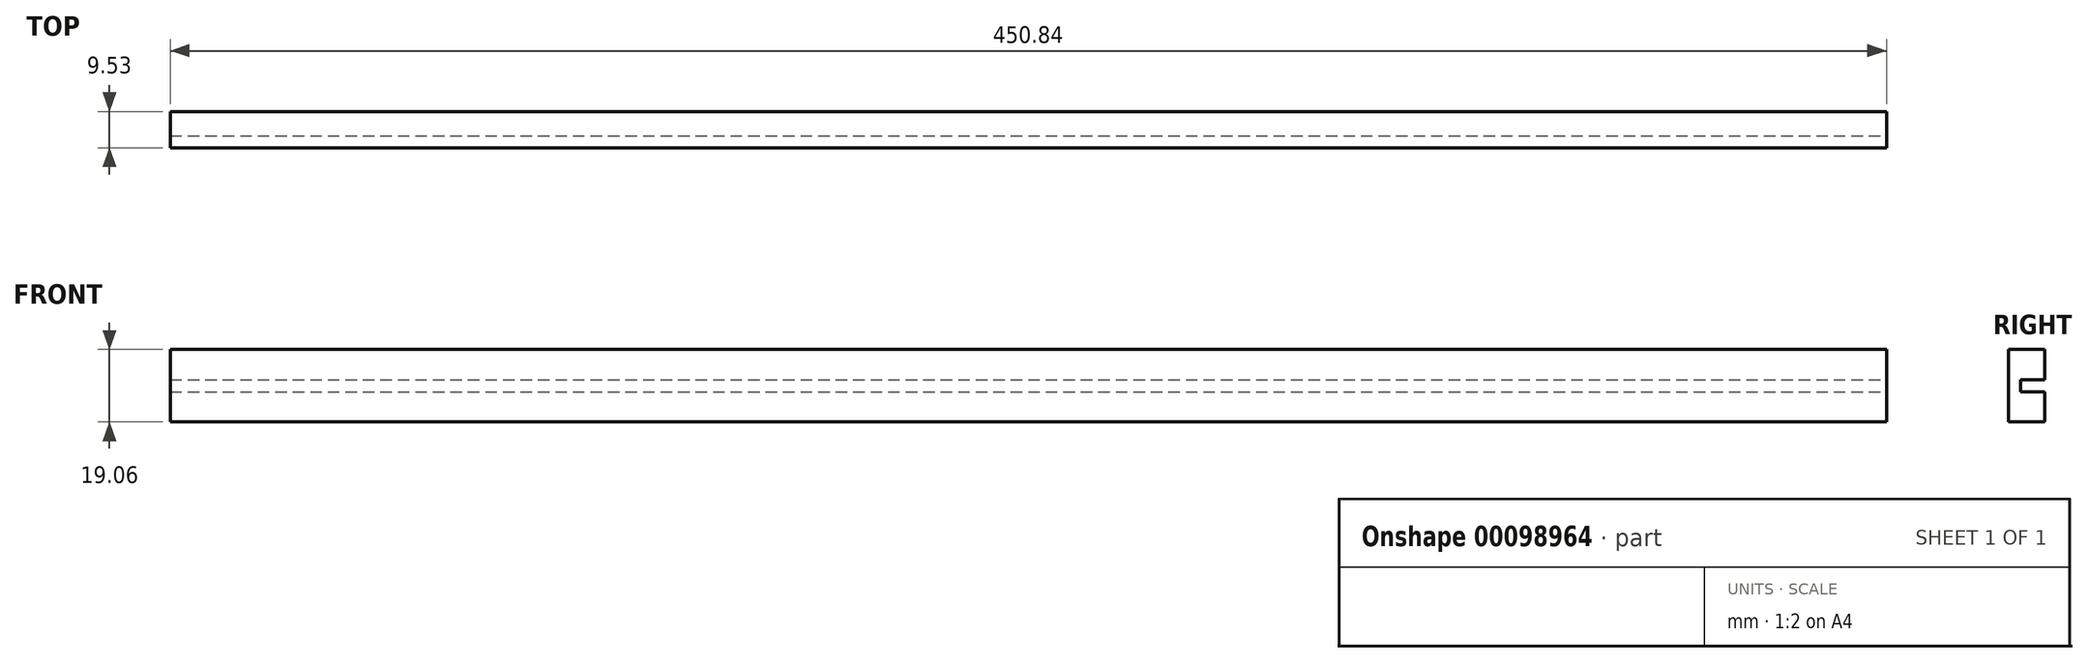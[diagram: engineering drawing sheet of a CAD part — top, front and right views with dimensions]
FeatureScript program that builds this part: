
annotation { "Feature Type Name" : "Feature", "Feature Type Description" : "" }
export const myFeature = defineFeature(function(context is Context, id is Id, definition is map)
    precondition{}
    {
        {
            var Q0;
            Q0=qCreatedBy(makeId("Front.planeOp"),FACE);
            var sketch = newSketch(context, id + "F0", { "sketchPlane" : qUnion([Q0])});
            skLineSegment(sketch, "E0.bottom", {"start": v(-225.43, 9.52) * mm, "end": v(225.43, 9.52) * mm});
            skLineSegment(sketch, "E0.top", {"start": v(-225.43, -9.52) * mm, "end": v(225.43, -9.52) * mm});
            skLineSegment(sketch, "E0.left", {"start": v(-225.43, 9.52) * mm, "end": v(-225.43, -9.52) * mm});
            skLineSegment(sketch, "E0.right", {"start": v(225.43, 9.52) * mm, "end": v(225.43, -9.52) * mm});
            skPoint(sketch, "E0.middle", {"position": v(0, 0) * mm});
            skLineSegment(sketch, "E1.bottom", {"start": v(-225.43, 1.59) * mm, "end": v(225.43, 1.59) * mm});
            skLineSegment(sketch, "E1.top", {"start": v(-225.43, -1.59) * mm, "end": v(225.43, -1.59) * mm});
            skLineSegment(sketch, "E1.left", {"start": v(-225.43, 1.59) * mm, "end": v(-225.43, -1.59) * mm});
            skLineSegment(sketch, "E1.right", {"start": v(225.43, 1.59) * mm, "end": v(225.43, -1.59) * mm});
            skSolve(sketch);
        }
        {
            var Q0;
            Q0 = qSketchRegion(id + "F0", true);
            extrude(context, id + "F1", {"entities" : qUnion([Q0]), "depth" : 9.52 * mm});
        }
        {
            var Q0;
            Q0=makeQuery(id+"F0.imprint","IMPRINT",FACE,{"disambiguationData":[TD([[makeQuery(id+"F0.imprint","IMPRINT",EDGE,{"derivedFrom":sQuery(id+"F0.wireOp",EDGE,"E1.bottom")}),-1.0]])]});
            extrude(context, id + "F2", {"entities" : qUnion([Q0]), "operationType" : NewBodyOperationType.REMOVE, "depth" : 6.35 * mm});
        }
    });
